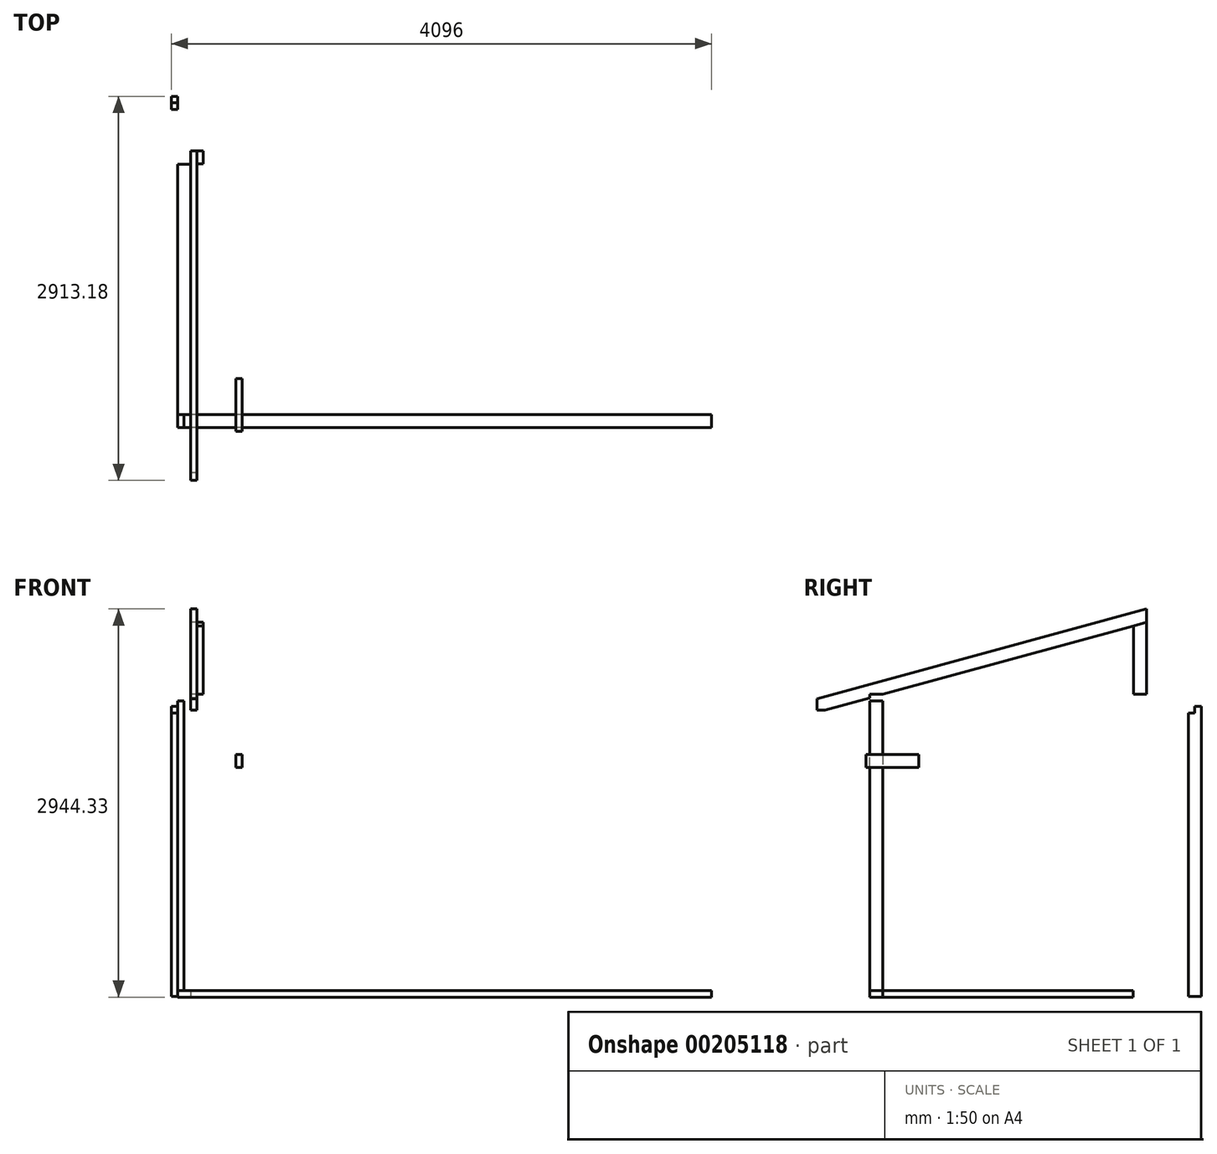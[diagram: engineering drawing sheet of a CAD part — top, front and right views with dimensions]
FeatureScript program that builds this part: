
annotation { "Feature Type Name" : "Feature", "Feature Type Description" : "" }
export const myFeature = defineFeature(function(context is Context, id is Id, definition is map)
    precondition{}
    {
        {
            var Q0;
            Q0=qCreatedBy(makeId("Right.planeOp"),FACE);
            var sketch = newSketch(context, id + "F0", { "sketchPlane" : qUnion([Q0])});
            skLineSegment(sketch, "E0", {"start": v(-372.34, -279.44) * mm, "end": v(-372.34, 1920.56) * mm});
            skLineSegment(sketch, "E1", {"start": v(-274.34, 1920.56) * mm, "end": v(-274.34, -279.44) * mm});
            skLineSegment(sketch, "E2", {"start": v(-274.34, -279.44) * mm, "end": v(-372.34, -279.44) * mm});
            skLineSegment(sketch, "E3", {"start": v(-372.34, 1920.56) * mm, "end": v(-274.34, 1920.56) * mm});
            skSolve(sketch);
        }
        {
            var Q0;
            Q0 = qSketchRegion(id + "F0", true);
            extrude(context, id + "F1", {"entities" : qUnion([Q0]), "depth" : 48 * mm});
        }
        {
            var Q0;
            Q0=qCreatedBy(makeId("Right.planeOp"),FACE);
            var sketch = newSketch(context, id + "F2", { "sketchPlane" : qUnion([Q0])});
            skLineSegment(sketch, "E4.bottom", {"start": v(-1006.13, 312.21) * mm, "end": v(-908.13, 312.21) * mm});
            skLineSegment(sketch, "E4.top", {"start": v(-1006.13, 264.21) * mm, "end": v(-908.13, 264.21) * mm});
            skLineSegment(sketch, "E4.left", {"start": v(-1006.13, 312.21) * mm, "end": v(-1006.13, 264.21) * mm});
            skLineSegment(sketch, "E4.right", {"start": v(-908.13, 312.21) * mm, "end": v(-908.13, 264.21) * mm});
            skSolve(sketch);
        }
        {
            var Q0;
            Q0=makeQuery(id+"F2.imprint","IMPRINT",FACE,{"disambiguationData":[TD([[makeQuery(id+"F2.imprint","IMPRINT",EDGE,{"derivedFrom":sQuery(id+"F2.wireOp",EDGE,"E4.bottom")}),-1.0]])]});
            extrude(context, id + "F3", {"entities" : qUnion([Q0]), "depth" : 4048 * mm});
        }
        {
            var Q0;
            Q0=qCreatedBy(makeId("Right.planeOp"),FACE);
            var sketch = newSketch(context, id + "F4", { "sketchPlane" : qUnion([Q0])});
            skLineSegment(sketch, "E5", {"start": v(-528.68, 1732.36) * mm, "end": v(-187.97, 1825.5) * mm});
            skLineSegment(sketch, "E6", {"start": v(1910.03, 2399.02) * mm, "end": v(1910.03, 2500.62) * mm});
            skLineSegment(sketch, "E7", {"start": v(1910.03, 2500.62) * mm, "end": v(-587.97, 1817.75) * mm});
            skLineSegment(sketch, "E8", {"start": v(-587.97, 1817.75) * mm, "end": v(-587.97, 1732.36) * mm});
            skLineSegment(sketch, "E9", {"start": v(-528.68, 1732.36) * mm, "end": v(-587.97, 1732.36) * mm});
            skLineSegment(sketch, "E10", {"start": v(-528.68, 1732.36) * mm, "end": v(1372.43, 1732.36) * mm, "construction": true});
            skLineSegment(sketch, "E11", {"start": v(-187.97, 1825.5) * mm, "end": v(-187.97, 1852.29) * mm});
            skLineSegment(sketch, "E12", {"start": v(-187.97, 1852.29) * mm, "end": v(-89.97, 1852.29) * mm});
            skLineSegment(sketch, "E13.trimOffspring", {"start": v(-89.97, 1852.29) * mm, "end": v(1910.03, 2399.02) * mm});
            skSolve(sketch);
        }
        {
            var Q0;
            Q0 = qSketchRegion(id + "F4", true);
            extrude(context, id + "F5", {"entities" : qUnion([Q0]), "depth" : 48 * mm});
        }
        {
            var Q0;
            Q0=makeQuery(id+"F3.opExtrude","SWEPT_BODY",BODY,{"disambiguationData":[OSD([sQuery(id+"F2.wireOp",EDGE,"E4.bottom"),sQuery(id+"F2.wireOp",EDGE,"E4.top"),sQuery(id+"F2.wireOp",EDGE,"E4.left"),sQuery(id+"F2.wireOp",EDGE,"E4.right")])]});
            transform(context, id + "F6", {"entities" : qUnion([Q0]), "transformType" : TransformType.TRANSLATION_3D, "dx" : 0 * mm, "dy" : 640 * mm, "dz" : -610 * mm, "makeCopy" : false});
        }
        {
            var Q0;
            Q0=qCreatedBy(makeId("Front.planeOp"),FACE);
            var sketch = newSketch(context, id + "F7", { "sketchPlane" : qUnion([Q0])});
            skLineSegment(sketch, "E14.bottom", {"start": v(2914.1, -253.15) * mm, "end": v(3012.1, -253.15) * mm});
            skLineSegment(sketch, "E14.top", {"start": v(2914.1, -301.15) * mm, "end": v(3012.1, -301.15) * mm});
            skLineSegment(sketch, "E14.left", {"start": v(2914.1, -253.15) * mm, "end": v(2914.1, -301.15) * mm});
            skLineSegment(sketch, "E14.right", {"start": v(3012.1, -253.15) * mm, "end": v(3012.1, -301.15) * mm});
            skSolve(sketch);
        }
        {
            var Q0;
            Q0 = qSketchRegion(id + "F7", true);
            extrude(context, id + "F8", {"entities" : qUnion([Q0]), "oppositeDirection" : true, "depth" : 1900 * mm});
        }
        {
            var Q0;
            Q0=makeQuery(id+"F3.opExtrude","SWEPT_BODY",BODY,{"disambiguationData":[OSD([sQuery(id+"F2.wireOp",EDGE,"E4.bottom"),sQuery(id+"F2.wireOp",EDGE,"E4.top"),sQuery(id+"F2.wireOp",EDGE,"E4.left"),sQuery(id+"F2.wireOp",EDGE,"E4.right")])]});
            transform(context, id + "F9", {"entities" : qUnion([Q0]), "transformType" : TransformType.TRANSLATION_3D, "dx" : 0 * mm, "dy" : 0 * mm, "dz" : -640 * mm, "makeCopy" : false});
        }
        {
            var Q0;
            Q0=makeQuery(id+"F3.opExtrude","SWEPT_BODY",BODY,{"disambiguationData":[OSD([sQuery(id+"F2.wireOp",EDGE,"E4.bottom"),sQuery(id+"F2.wireOp",EDGE,"E4.top"),sQuery(id+"F2.wireOp",EDGE,"E4.left"),sQuery(id+"F2.wireOp",EDGE,"E4.right")])]});
            var Q1;
            Q1=makeQuery(id+"F3.opExtrude","CAP_VERTEX",VERTEX,{"disambiguationData":[OSD([sQuery(id+"F2.wireOp",EDGE,"E4.bottom"),sQuery(id+"F2.wireOp",EDGE,"E4.left")])],"isStart":true});
            var Q2;
            Q2=makeQuery(id+"F1.opExtrude","CAP_VERTEX",VERTEX,{"disambiguationData":[OSD([sQuery(id+"F0.wireOp",EDGE,"E0"),sQuery(id+"F0.wireOp",EDGE,"E2")])],"isStart":true});
            transform(context, id + "F10", {"entities" : qUnion([Q0]), "transformType" : TransformType.TRANSLATION_ENTITY, "oppositeDirectionEntity" : false, "transformLine" : qUnion([Q1, Q2]), "makeCopy" : false});
        }
        {
            var Q0;
            Q0=makeQuery(id+"F5.opExtrude","SWEPT_BODY",BODY,{"disambiguationData":[OSD([sQuery(id+"F4.wireOp",EDGE,"E5"),sQuery(id+"F4.wireOp",EDGE,"E6"),sQuery(id+"F4.wireOp",EDGE,"E7"),sQuery(id+"F4.wireOp",EDGE,"E8"),sQuery(id+"F4.wireOp",EDGE,"E9"),sQuery(id+"F4.wireOp",EDGE,"E11"),sQuery(id+"F4.wireOp",EDGE,"E12"),sQuery(id+"F4.wireOp",EDGE,"E13.trimOffspring")])]});
            var Q1;
            Q1=makeQuery(id+"F5.opExtrude","CAP_VERTEX",VERTEX,{"disambiguationData":[OSD([sQuery(id+"F4.wireOp",EDGE,"E12"),sQuery(id+"F4.wireOp",EDGE,"E13.trimOffspring")])],"isStart":true});
            var Q2;
            Q2=makeQuery(id+"F1.opExtrude","CAP_VERTEX",VERTEX,{"disambiguationData":[OSD([sQuery(id+"F0.wireOp",EDGE,"E1"),sQuery(id+"F0.wireOp",EDGE,"E3")])],"isStart":true});
            transform(context, id + "F11", {"entities" : qUnion([Q0]), "transformType" : TransformType.TRANSLATION_ENTITY, "oppositeDirectionEntity" : false, "transformLine" : qUnion([Q1, Q2]), "makeCopy" : false});
        }
        {
            var Q0;
            Q0=makeQuery(id+"F8.opExtrude","SWEPT_BODY",BODY,{"disambiguationData":[OSD([sQuery(id+"F7.wireOp",EDGE,"E14.bottom"),sQuery(id+"F7.wireOp",EDGE,"E14.top"),sQuery(id+"F7.wireOp",EDGE,"E14.left"),sQuery(id+"F7.wireOp",EDGE,"E14.right")])]});
            var Q1;
            Q1=makeQuery(id+"F8.opExtrude","CAP_VERTEX",VERTEX,{"disambiguationData":[OSD([sQuery(id+"F7.wireOp",EDGE,"E14.bottom"),sQuery(id+"F7.wireOp",EDGE,"E14.left")])],"isStart":true});
            var Q2;
            Q2=makeQuery(id+"F3.opExtrude","CAP_VERTEX",VERTEX,{"disambiguationData":[OSD([sQuery(id+"F2.wireOp",EDGE,"E4.bottom"),sQuery(id+"F2.wireOp",EDGE,"E4.right")])],"isStart":true});
            transform(context, id + "F12", {"entities" : qUnion([Q0]), "transformType" : TransformType.TRANSLATION_ENTITY, "oppositeDirectionEntity" : false, "transformLine" : qUnion([Q1, Q2]), "makeCopy" : false});
        }
        {
            var Q0;
            Q0=makeQuery(id+"F5.opExtrude","SWEPT_BODY",BODY,{"disambiguationData":[OSD([sQuery(id+"F4.wireOp",EDGE,"E5"),sQuery(id+"F4.wireOp",EDGE,"E6"),sQuery(id+"F4.wireOp",EDGE,"E7"),sQuery(id+"F4.wireOp",EDGE,"E8"),sQuery(id+"F4.wireOp",EDGE,"E9"),sQuery(id+"F4.wireOp",EDGE,"E11"),sQuery(id+"F4.wireOp",EDGE,"E12"),sQuery(id+"F4.wireOp",EDGE,"E13.trimOffspring")])]});
            transform(context, id + "F13", {"entities" : qUnion([Q0]), "transformType" : TransformType.TRANSLATION_3D, "dx" : 0 * mm, "dy" : 0 * mm, "dz" : 48 * mm, "makeCopy" : false});
        }
        {
            var Q0;
            Q0=makeQuery(id+"F5.opExtrude","SWEPT_BODY",BODY,{"disambiguationData":[OSD([sQuery(id+"F4.wireOp",EDGE,"E5"),sQuery(id+"F4.wireOp",EDGE,"E6"),sQuery(id+"F4.wireOp",EDGE,"E7"),sQuery(id+"F4.wireOp",EDGE,"E8"),sQuery(id+"F4.wireOp",EDGE,"E9"),sQuery(id+"F4.wireOp",EDGE,"E11"),sQuery(id+"F4.wireOp",EDGE,"E12"),sQuery(id+"F4.wireOp",EDGE,"E13.trimOffspring")])]});
            transform(context, id + "F14", {"entities" : qUnion([Q0]), "transformType" : TransformType.TRANSLATION_3D, "dx" : 98 * mm, "dy" : 0 * mm, "dz" : 0 * mm, "makeCopy" : false});
        }
        {
            var Q0;
            Q0=makeQuery(id+"F5.opExtrude","CAP_FACE",FACE,{"disambiguationData":[OSD([sQuery(id+"F4.wireOp",EDGE,"E5"),sQuery(id+"F4.wireOp",EDGE,"E6"),sQuery(id+"F4.wireOp",EDGE,"E7"),sQuery(id+"F4.wireOp",EDGE,"E8"),sQuery(id+"F4.wireOp",EDGE,"E9"),sQuery(id+"F4.wireOp",EDGE,"E11"),sQuery(id+"F4.wireOp",EDGE,"E12"),sQuery(id+"F4.wireOp",EDGE,"E13.trimOffspring")])],"isStart":false});
            var sketch = newSketch(context, id + "F15", { "sketchPlane" : qUnion([Q0])});
            skLineSegment(sketch, "E15", {"start": v(-370.91, 2043.76) * mm, "end": v(1725.66, 2616.9) * mm});
            skLineSegment(sketch, "E16", {"start": v(1725.66, 2616.9) * mm, "end": v(1725.66, 2861.87) * mm});
            skLineSegment(sketch, "E17", {"start": v(1725.66, 2861.87) * mm, "end": v(-370.91, 2861.87) * mm});
            skLineSegment(sketch, "E18", {"start": v(-370.91, 2861.87) * mm, "end": v(-370.91, 2043.76) * mm});
            skSolve(sketch);
        }
        {
            var Q0;
            Q0=makeQuery(id+"F15.imprint","IMPRINT",FACE,{"disambiguationData":[TD([[makeQuery(id+"F15.imprint","IMPRINT",EDGE,{"derivedFrom":sQuery(id+"F15.wireOp",EDGE,"E15")}),-1.0]])]});
            extrude(context, id + "F16", {"entities" : qUnion([Q0]), "operationType" : NewBodyOperationType.REMOVE, "oppositeDirection" : true, "depth" : 390 * mm});
        }
        {
            var Q0;
            Q0=qCreatedBy(makeId("Front.planeOp"),FACE);
            var sketch = newSketch(context, id + "F17", { "sketchPlane" : qUnion([Q0])});
            skLineSegment(sketch, "E19.bottom", {"start": v(441.1, 1512.34) * mm, "end": v(489.1, 1512.34) * mm});
            skLineSegment(sketch, "E19.top", {"start": v(441.1, 1414.34) * mm, "end": v(489.1, 1414.34) * mm});
            skLineSegment(sketch, "E19.left", {"start": v(441.1, 1512.34) * mm, "end": v(441.1, 1414.34) * mm});
            skLineSegment(sketch, "E19.right", {"start": v(489.1, 1512.34) * mm, "end": v(489.1, 1414.34) * mm});
            skSolve(sketch);
        }
        {
            var Q0;
            Q0 = qSketchRegion(id + "F17", true);
            extrude(context, id + "F18", {"entities" : qUnion([Q0]), "depth" : 400 * mm});
        }
        {
            var Q0;
            Q0=makeQuery(id+"F5.opExtrude","CAP_FACE",FACE,{"disambiguationData":[OSD([sQuery(id+"F4.wireOp",EDGE,"E5"),sQuery(id+"F4.wireOp",EDGE,"E6"),sQuery(id+"F4.wireOp",EDGE,"E7"),sQuery(id+"F4.wireOp",EDGE,"E8"),sQuery(id+"F4.wireOp",EDGE,"E9"),sQuery(id+"F4.wireOp",EDGE,"E11"),sQuery(id+"F4.wireOp",EDGE,"E12"),sQuery(id+"F4.wireOp",EDGE,"E13.trimOffspring")])],"isStart":false});
            var sketch = newSketch(context, id + "F19", { "sketchPlane" : qUnion([Q0])});
            skLineSegment(sketch, "E20", {"start": v(-274.34, 1968.56) * mm, "end": v(1861.37, 1968.56) * mm, "construction": true});
            skLineSegment(sketch, "E21", {"start": v(1725.66, 2515.3) * mm, "end": v(1725.66, 1968.56) * mm});
            skLineSegment(sketch, "E22", {"start": v(1725.66, 1968.56) * mm, "end": v(1627.66, 1968.56) * mm});
            skLineSegment(sketch, "E23", {"start": v(1627.66, 1968.56) * mm, "end": v(1627.66, 2488.5) * mm});
            skLineSegment(sketch, "E24", {"start": v(1627.66, 2488.5) * mm, "end": v(1725.66, 2515.3) * mm});
            skSolve(sketch);
        }
        {
            var Q0;
            Q0=makeQuery(id+"F19.imprint","IMPRINT",FACE,{"disambiguationData":[TD([[makeQuery(id+"F19.imprint","IMPRINT",EDGE,{"derivedFrom":sQuery(id+"F19.wireOp",EDGE,"E21")}),-1.0]])]});
            extrude(context, id + "F20", {"entities" : qUnion([Q0]), "depth" : 48 * mm});
        }
        {
            var Q0;
            Q0=makeQuery(id+"F8.opExtrude","SWEPT_FACE",FACE,{"disambiguationData":[OSD([sQuery(id+"F7.wireOp",EDGE,"E14.left")])]});
            var sketch = newSketch(context, id + "F21", { "sketchPlane" : qUnion([Q0])});
            skLineSegment(sketch, "E25.bottom", {"start": v(-2042.84, -321.78) * mm, "end": v(-2140.84, -321.78) * mm});
            skLineSegment(sketch, "E25.top", {"start": v(-2091.84, 1878.22) * mm, "end": v(-2140.84, 1878.22) * mm});
            skLineSegment(sketch, "E25.left", {"start": v(-2042.84, -321.78) * mm, "end": v(-2042.84, 1828.22) * mm});
            skLineSegment(sketch, "E25.right", {"start": v(-2140.84, -321.78) * mm, "end": v(-2140.84, 1878.22) * mm});
            skLineSegment(sketch, "E26", {"start": v(-2091.84, 1878.22) * mm, "end": v(-2091.84, 1828.22) * mm});
            skLineSegment(sketch, "E27", {"start": v(-2091.84, 1828.22) * mm, "end": v(-2042.84, 1828.22) * mm});
            skPoint(sketch, "E28.orphan", {"position": v(-2042.84, 1878.22) * mm});
            skSolve(sketch);
        }
        {
            var Q0;
            Q0=makeQuery(id+"F21.imprint","IMPRINT",FACE,{"disambiguationData":[TD([[makeQuery(id+"F21.imprint","IMPRINT",EDGE,{"derivedFrom":sQuery(id+"F21.wireOp",EDGE,"E25.bottom")}),-1.0]])]});
            extrude(context, id + "F22", {"entities" : qUnion([Q0]), "depth" : 48 * mm});
        }
    });
